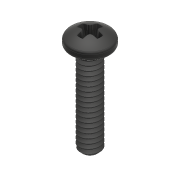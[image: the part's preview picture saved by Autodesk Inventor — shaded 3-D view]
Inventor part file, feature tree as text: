
AUTODESK INVENTOR PART (.ipt)
format: ipt  version: 2017 (Build 210142000, 142)  size: 1,221,632 bytes
history: native  units: mm
features: fillet x1
ambient origin geometry x8: Origin, YZ Plane, XZ Plane, XY Plane, X Axis, Y Axis, Z Axis, Center Point
bodies: Solid1 (feature_tree)
feature tree (1):
  fillet  "Fillet1"  [1 undecoded]
note: 1 required parameter value undecoded (feature->parameter linkage not recoverable at this tier; creation-order binding heuristic only, values carry confidence <= 0.55)
